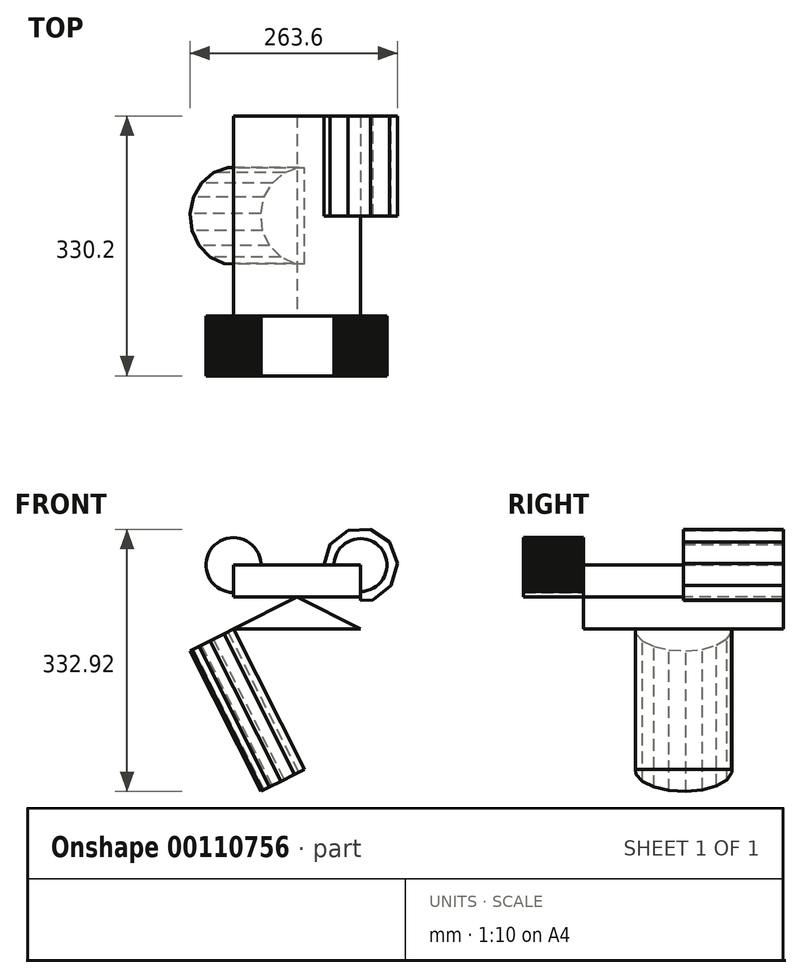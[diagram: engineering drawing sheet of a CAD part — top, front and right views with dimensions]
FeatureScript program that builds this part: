
annotation { "Feature Type Name" : "Feature", "Feature Type Description" : "" }
export const myFeature = defineFeature(function(context is Context, id is Id, definition is map)
    precondition{}
    {
        {
            var Q0;
            Q0=qCreatedBy(makeId("Front.planeOp"),FACE);
            var sketch = newSketch(context, id + "F0", { "sketchPlane" : qUnion([Q0])});
            skLineSegment(sketch, "E0", {"start": v(0, 0) * mm, "end": v(-161.37, 0) * mm});
            skLineSegment(sketch, "E1", {"start": v(-161.37, 0) * mm, "end": v(-161.37, -81.28) * mm});
            skLineSegment(sketch, "E2", {"start": v(-161.37, -81.28) * mm, "end": v(0, -81.28) * mm});
            skLineSegment(sketch, "E3", {"start": v(0, -81.28) * mm, "end": v(0, 0) * mm});
            skSolve(sketch);
        }
        {
            var Q0;
            Q0=makeQuery(id+"F0.imprint","IMPRINT",FACE,{"disambiguationData":[TD([[makeQuery(id+"F0.imprint","IMPRINT",EDGE,{"derivedFrom":sQuery(id+"F0.wireOp",EDGE,"E0")}),1.0]])]});
            var sketch = newSketch(context, id + "F1", { "sketchPlane" : qUnion([Q0])});
            skSolve(sketch);
        }
        {
            var Q0;
            Q0=makeQuery(id+"F0.imprint","IMPRINT",FACE,{"disambiguationData":[TD([[makeQuery(id+"F0.imprint","IMPRINT",EDGE,{"derivedFrom":sQuery(id+"F0.wireOp",EDGE,"E0")}),1.0]])]});
            extrude(context, id + "F2", {"entities" : qUnion([Q0]), "depth" : 254 * mm});
        }
        {
            var Q0;
            Q0=makeQuery(id+"F2.opExtrude","CAP_FACE",FACE,{"disambiguationData":[OSD([sQuery(id+"F0.wireOp",EDGE,"E0"),sQuery(id+"F0.wireOp",EDGE,"E1"),sQuery(id+"F0.wireOp",EDGE,"E2"),sQuery(id+"F0.wireOp",EDGE,"E3")])],"isStart":false});
            var sketch = newSketch(context, id + "F3", { "sketchPlane" : qUnion([Q0])});
            skLineSegment(sketch, "E4", {"start": v(-161.37, -81.28) * mm, "end": v(-161.37, -40.64) * mm});
            skLineSegment(sketch, "E5", {"start": v(-161.37, -40.64) * mm, "end": v(0, -40.64) * mm});
            skLineSegment(sketch, "E6", {"start": v(0, -40.64) * mm, "end": v(0, -81.28) * mm});
            skLineSegment(sketch, "E7", {"start": v(0, -81.28) * mm, "end": v(-80.69, -40.64) * mm});
            skLineSegment(sketch, "E8", {"start": v(-80.69, -40.64) * mm, "end": v(-161.37, -81.28) * mm});
            skSolve(sketch);
        }
        {
            var Q0;
            {var subQ0=sQuery(id+"F3.wireOp",EDGE,"E4");Q0=makeQuery(id+"F3.imprint","IMPRINT",FACE,{"disambiguationData":[TD([[makeQuery(id+"F3.imprint","IMPRINT",EDGE,{"derivedFrom":subQ0}),1.0]])]});}
            extrude(context, id + "F4", {"entities" : qUnion([Q0]), "operationType" : NewBodyOperationType.REMOVE, "endBound" : BoundingType.THROUGH_ALL, "oppositeDirection" : true, "depth" : 25.4 * mm});
        }
        {
            var Q0;
            Q0=makeQuery(id+"F2.opExtrude","CAP_FACE",FACE,{"disambiguationData":[OSD([sQuery(id+"F0.wireOp",EDGE,"E0"),sQuery(id+"F0.wireOp",EDGE,"E1"),sQuery(id+"F0.wireOp",EDGE,"E2"),sQuery(id+"F0.wireOp",EDGE,"E3")])],"isStart":false});
            var sketch = newSketch(context, id + "F5", { "sketchPlane" : qUnion([Q0])});
            skLineSegment(sketch, "E9", {"start": v(-80.69, -40.64) * mm, "end": v(0, -81.28) * mm});
            skLineSegment(sketch, "E10", {"start": v(0, -81.28) * mm, "end": v(0, -40.64) * mm});
            skLineSegment(sketch, "E11", {"start": v(0, -40.64) * mm, "end": v(-80.69, -40.64) * mm});
            skSolve(sketch);
        }
        {
            var Q0;
            Q0=makeQuery(id+"F5.imprint","IMPRINT",FACE,{"disambiguationData":[TD([[makeQuery(id+"F5.imprint","IMPRINT",EDGE,{"derivedFrom":sQuery(id+"F5.wireOp",EDGE,"E9")}),1.0]])]});
            extrude(context, id + "F6", {"entities" : qUnion([Q0]), "operationType" : NewBodyOperationType.REMOVE, "endBound" : BoundingType.THROUGH_ALL, "oppositeDirection" : true, "depth" : 25.4 * mm});
        }
        {
            var Q0;
            {var subQ0=sQuery(id+"F0.wireOp",EDGE,"E1");var subQ1=sQuery(id+"F0.wireOp",EDGE,"E3");var subQ2=sQuery(id+"F0.wireOp",EDGE,"E0");Q0=makeQuery(id+"F6.boolean.opBoolean","SPLIT",FACE,{"disambiguationData":[TD([makeQuery(id+"F2.opExtrude","SWEPT_FACE",FACE,{"disambiguationData":[OSD([subQ2])]})])],"derivedFrom":makeQuery(id+"F2.opExtrude","CAP_FACE",FACE,{"disambiguationData":[OSD([subQ2,subQ0,sQuery(id+"F0.wireOp",EDGE,"E2"),subQ1])],"isStart":false})});}
            var sketch = newSketch(context, id + "F7", { "sketchPlane" : qUnion([Q0])});
            skSolve(sketch);
        }
        {
            var Q0;
            Q0=makeQuery(id+"F7.imprint","IMPRINT",FACE,{"disambiguationData":[TD([[makeQuery(id+"F7.imprint","IMPRINT",EDGE,{"derivedFrom":makeQuery(id+"F2.opExtrude","CAP_EDGE",EDGE,{"disambiguationData":[OSD([sQuery(id+"F0.wireOp",EDGE,"E0")])],"isStart":false})}),1.0]])]});
            var sketch = newSketch(context, id + "F8", { "sketchPlane" : qUnion([Q0])});
            skCircle(sketch, "E12.cCircle", {"center": v(0, 0) * mm, "radius": 33.51 * mm, "construction": true});
            skLineSegment(sketch, "E12.0", {"start": v(-33.51, -2.1) * mm, "end": v(-33.51, 2.1) * mm});
            skLineSegment(sketch, "E12.1", {"start": v(-33.51, 2.1) * mm, "end": v(-32.99, 6.3) * mm});
            skLineSegment(sketch, "E12.2", {"start": v(-32.99, 6.3) * mm, "end": v(-31.94, 10.38) * mm});
            skLineSegment(sketch, "E12.3", {"start": v(-31.94, 10.38) * mm, "end": v(-30.38, 14.3) * mm});
            skLineSegment(sketch, "E12.4", {"start": v(-30.38, 14.3) * mm, "end": v(-28.35, 18) * mm});
            skLineSegment(sketch, "E12.5", {"start": v(-28.35, 18) * mm, "end": v(-25.87, 21.4) * mm});
            skLineSegment(sketch, "E12.6", {"start": v(-25.87, 21.4) * mm, "end": v(-22.99, 24.48) * mm});
            skLineSegment(sketch, "E12.7", {"start": v(-22.99, 24.48) * mm, "end": v(-19.74, 27.17) * mm});
            skLineSegment(sketch, "E12.8", {"start": v(-19.74, 27.17) * mm, "end": v(-16.18, 29.43) * mm});
            skLineSegment(sketch, "E12.9", {"start": v(-16.18, 29.43) * mm, "end": v(-12.36, 31.22) * mm});
            skLineSegment(sketch, "E12.10", {"start": v(-12.36, 31.22) * mm, "end": v(-8.35, 32.53) * mm});
            skLineSegment(sketch, "E12.11", {"start": v(-8.35, 32.53) * mm, "end": v(-4.2, 33.32) * mm});
            skLineSegment(sketch, "E12.12", {"start": v(-4.2, 33.32) * mm, "end": v(0, 33.58) * mm});
            skLineSegment(sketch, "E12.13", {"start": v(0, 33.58) * mm, "end": v(4.2, 33.32) * mm});
            skLineSegment(sketch, "E12.14", {"start": v(4.2, 33.32) * mm, "end": v(8.35, 32.53) * mm});
            skLineSegment(sketch, "E12.15", {"start": v(8.35, 32.53) * mm, "end": v(12.36, 31.22) * mm});
            skLineSegment(sketch, "E12.16", {"start": v(12.36, 31.22) * mm, "end": v(16.18, 29.43) * mm});
            skLineSegment(sketch, "E12.17", {"start": v(16.18, 29.43) * mm, "end": v(19.74, 27.17) * mm});
            skLineSegment(sketch, "E12.18", {"start": v(19.74, 27.17) * mm, "end": v(22.99, 24.48) * mm});
            skLineSegment(sketch, "E12.19", {"start": v(22.99, 24.48) * mm, "end": v(25.87, 21.4) * mm});
            skLineSegment(sketch, "E12.20", {"start": v(25.87, 21.4) * mm, "end": v(28.35, 18) * mm});
            skLineSegment(sketch, "E12.21", {"start": v(28.35, 18) * mm, "end": v(30.38, 14.3) * mm});
            skLineSegment(sketch, "E12.22", {"start": v(30.38, 14.3) * mm, "end": v(31.94, 10.38) * mm});
            skLineSegment(sketch, "E12.23", {"start": v(31.94, 10.38) * mm, "end": v(32.99, 6.3) * mm});
            skLineSegment(sketch, "E12.24", {"start": v(32.99, 6.3) * mm, "end": v(33.51, 2.1) * mm});
            skLineSegment(sketch, "E12.25", {"start": v(33.51, 2.1) * mm, "end": v(33.51, -2.1) * mm});
            skLineSegment(sketch, "E12.26", {"start": v(33.51, -2.1) * mm, "end": v(32.99, -6.3) * mm});
            skLineSegment(sketch, "E12.27", {"start": v(32.99, -6.3) * mm, "end": v(31.94, -10.38) * mm});
            skLineSegment(sketch, "E12.28", {"start": v(31.94, -10.38) * mm, "end": v(30.38, -14.3) * mm});
            skLineSegment(sketch, "E12.29", {"start": v(30.38, -14.3) * mm, "end": v(28.35, -18) * mm});
            skLineSegment(sketch, "E12.30", {"start": v(28.35, -18) * mm, "end": v(25.87, -21.4) * mm});
            skLineSegment(sketch, "E12.31", {"start": v(25.87, -21.4) * mm, "end": v(22.99, -24.48) * mm});
            skLineSegment(sketch, "E12.32", {"start": v(22.99, -24.48) * mm, "end": v(19.74, -27.17) * mm});
            skLineSegment(sketch, "E12.33", {"start": v(19.74, -27.17) * mm, "end": v(16.18, -29.43) * mm});
            skLineSegment(sketch, "E12.34", {"start": v(16.18, -29.43) * mm, "end": v(12.36, -31.22) * mm});
            skLineSegment(sketch, "E12.35", {"start": v(12.36, -31.22) * mm, "end": v(8.35, -32.53) * mm});
            skLineSegment(sketch, "E12.36", {"start": v(8.35, -32.53) * mm, "end": v(4.2, -33.32) * mm});
            skLineSegment(sketch, "E12.37", {"start": v(4.2, -33.32) * mm, "end": v(0, -33.58) * mm});
            skLineSegment(sketch, "E12.38", {"start": v(0, -33.58) * mm, "end": v(-4.2, -33.32) * mm});
            skLineSegment(sketch, "E12.39", {"start": v(-4.2, -33.32) * mm, "end": v(-8.35, -32.53) * mm});
            skLineSegment(sketch, "E12.40", {"start": v(-8.35, -32.53) * mm, "end": v(-12.36, -31.22) * mm});
            skLineSegment(sketch, "E12.41", {"start": v(-12.36, -31.22) * mm, "end": v(-16.18, -29.43) * mm});
            skLineSegment(sketch, "E12.42", {"start": v(-16.18, -29.43) * mm, "end": v(-19.74, -27.17) * mm});
            skLineSegment(sketch, "E12.43", {"start": v(-19.74, -27.17) * mm, "end": v(-22.99, -24.48) * mm});
            skLineSegment(sketch, "E12.44", {"start": v(-22.99, -24.48) * mm, "end": v(-25.87, -21.4) * mm});
            skLineSegment(sketch, "E12.45", {"start": v(-25.87, -21.4) * mm, "end": v(-28.35, -18) * mm});
            skLineSegment(sketch, "E12.46", {"start": v(-28.35, -18) * mm, "end": v(-30.38, -14.3) * mm});
            skLineSegment(sketch, "E12.47", {"start": v(-30.38, -14.3) * mm, "end": v(-31.94, -10.38) * mm});
            skLineSegment(sketch, "E12.48", {"start": v(-31.94, -10.38) * mm, "end": v(-32.99, -6.3) * mm});
            skLineSegment(sketch, "E12.49", {"start": v(-32.99, -6.3) * mm, "end": v(-33.51, -2.1) * mm});
            skPoint(sketch, "E12.0.midPoint", {"position": v(-33.51, 0) * mm});
            skSolve(sketch);
        }
        {
            var Q0;
            {var subQ1=sQuery(id+"F8.wireOp",EDGE,"E12.1");Q0=makeQuery(id+"F8.imprint","IMPRINT",FACE,{"disambiguationData":[TD([[makeQuery(id+"F8.imprint","IMPRINT",EDGE,{"derivedFrom":subQ1}),-1.0]])]});}
            extrude(context, id + "F9", {"entities" : qUnion([Q0]), "depth" : 76.2 * mm});
        }
        {
            var Q0;
            Q0=makeQuery(id+"F7.imprint","IMPRINT",FACE,{"disambiguationData":[TD([[makeQuery(id+"F7.imprint","IMPRINT",EDGE,{"derivedFrom":makeQuery(id+"F2.opExtrude","CAP_EDGE",EDGE,{"disambiguationData":[OSD([sQuery(id+"F0.wireOp",EDGE,"E0")])],"isStart":false})}),1.0]])]});
            var sketch = newSketch(context, id + "F10", { "sketchPlane" : qUnion([Q0])});
            skCircle(sketch, "E13.cCircle", {"center": v(-161.48, 0) * mm, "radius": 34.82 * mm, "construction": true});
            skLineSegment(sketch, "E13.0", {"start": v(-126.66, 2.2) * mm, "end": v(-126.66, -2.2) * mm});
            skLineSegment(sketch, "E13.1", {"start": v(-126.66, -2.2) * mm, "end": v(-127.21, -6.54) * mm});
            skLineSegment(sketch, "E13.2", {"start": v(-127.21, -6.54) * mm, "end": v(-128.3, -10.78) * mm});
            skLineSegment(sketch, "E13.3", {"start": v(-128.3, -10.78) * mm, "end": v(-129.91, -14.85) * mm});
            skLineSegment(sketch, "E13.4", {"start": v(-129.91, -14.85) * mm, "end": v(-132.02, -18.7) * mm});
            skLineSegment(sketch, "E13.5", {"start": v(-132.02, -18.7) * mm, "end": v(-134.6, -22.24) * mm});
            skLineSegment(sketch, "E13.6", {"start": v(-134.6, -22.24) * mm, "end": v(-137.6, -25.43) * mm});
            skLineSegment(sketch, "E13.7", {"start": v(-137.6, -25.43) * mm, "end": v(-140.97, -28.22) * mm});
            skLineSegment(sketch, "E13.8", {"start": v(-140.97, -28.22) * mm, "end": v(-144.67, -30.57) * mm});
            skLineSegment(sketch, "E13.9", {"start": v(-144.67, -30.57) * mm, "end": v(-148.64, -32.44) * mm});
            skLineSegment(sketch, "E13.10", {"start": v(-148.64, -32.44) * mm, "end": v(-152.8, -33.79) * mm});
            skLineSegment(sketch, "E13.11", {"start": v(-152.8, -33.79) * mm, "end": v(-157.1, -34.61) * mm});
            skLineSegment(sketch, "E13.12", {"start": v(-157.1, -34.61) * mm, "end": v(-161.48, -34.89) * mm});
            skLineSegment(sketch, "E13.13", {"start": v(-161.48, -34.89) * mm, "end": v(-165.85, -34.61) * mm});
            skLineSegment(sketch, "E13.14", {"start": v(-165.85, -34.61) * mm, "end": v(-170.15, -33.79) * mm});
            skLineSegment(sketch, "E13.15", {"start": v(-170.15, -33.79) * mm, "end": v(-174.32, -32.44) * mm});
            skLineSegment(sketch, "E13.16", {"start": v(-174.32, -32.44) * mm, "end": v(-178.28, -30.57) * mm});
            skLineSegment(sketch, "E13.17", {"start": v(-178.28, -30.57) * mm, "end": v(-181.98, -28.22) * mm});
            skLineSegment(sketch, "E13.18", {"start": v(-181.98, -28.22) * mm, "end": v(-185.36, -25.43) * mm});
            skLineSegment(sketch, "E13.19", {"start": v(-185.36, -25.43) * mm, "end": v(-188.36, -22.24) * mm});
            skLineSegment(sketch, "E13.20", {"start": v(-188.36, -22.24) * mm, "end": v(-190.93, -18.7) * mm});
            skLineSegment(sketch, "E13.21", {"start": v(-190.93, -18.7) * mm, "end": v(-193.04, -14.85) * mm});
            skLineSegment(sketch, "E13.22", {"start": v(-193.04, -14.85) * mm, "end": v(-194.66, -10.78) * mm});
            skLineSegment(sketch, "E13.23", {"start": v(-194.66, -10.78) * mm, "end": v(-195.75, -6.54) * mm});
            skLineSegment(sketch, "E13.24", {"start": v(-195.75, -6.54) * mm, "end": v(-196.3, -2.2) * mm});
            skLineSegment(sketch, "E13.25", {"start": v(-196.3, -2.2) * mm, "end": v(-196.3, 2.2) * mm});
            skLineSegment(sketch, "E13.26", {"start": v(-196.3, 2.2) * mm, "end": v(-195.75, 6.54) * mm});
            skLineSegment(sketch, "E13.27", {"start": v(-195.75, 6.54) * mm, "end": v(-194.66, 10.78) * mm});
            skLineSegment(sketch, "E13.28", {"start": v(-194.66, 10.78) * mm, "end": v(-193.04, 14.85) * mm});
            skLineSegment(sketch, "E13.29", {"start": v(-193.04, 14.85) * mm, "end": v(-190.93, 18.7) * mm});
            skLineSegment(sketch, "E13.30", {"start": v(-190.93, 18.7) * mm, "end": v(-188.36, 22.24) * mm});
            skLineSegment(sketch, "E13.31", {"start": v(-188.36, 22.24) * mm, "end": v(-185.36, 25.43) * mm});
            skLineSegment(sketch, "E13.32", {"start": v(-185.36, 25.43) * mm, "end": v(-181.98, 28.22) * mm});
            skLineSegment(sketch, "E13.33", {"start": v(-181.98, 28.22) * mm, "end": v(-178.28, 30.57) * mm});
            skLineSegment(sketch, "E13.34", {"start": v(-178.28, 30.57) * mm, "end": v(-174.32, 32.44) * mm});
            skLineSegment(sketch, "E13.35", {"start": v(-174.32, 32.44) * mm, "end": v(-170.15, 33.79) * mm});
            skLineSegment(sketch, "E13.36", {"start": v(-170.15, 33.79) * mm, "end": v(-165.85, 34.61) * mm});
            skLineSegment(sketch, "E13.37", {"start": v(-165.85, 34.61) * mm, "end": v(-161.48, 34.89) * mm});
            skLineSegment(sketch, "E13.38", {"start": v(-161.48, 34.89) * mm, "end": v(-157.1, 34.61) * mm});
            skLineSegment(sketch, "E13.39", {"start": v(-157.1, 34.61) * mm, "end": v(-152.8, 33.79) * mm});
            skLineSegment(sketch, "E13.40", {"start": v(-152.8, 33.79) * mm, "end": v(-148.64, 32.44) * mm});
            skLineSegment(sketch, "E13.41", {"start": v(-148.64, 32.44) * mm, "end": v(-144.67, 30.57) * mm});
            skLineSegment(sketch, "E13.42", {"start": v(-144.67, 30.57) * mm, "end": v(-140.97, 28.22) * mm});
            skLineSegment(sketch, "E13.43", {"start": v(-140.97, 28.22) * mm, "end": v(-137.6, 25.43) * mm});
            skLineSegment(sketch, "E13.44", {"start": v(-137.6, 25.43) * mm, "end": v(-134.6, 22.24) * mm});
            skLineSegment(sketch, "E13.45", {"start": v(-134.6, 22.24) * mm, "end": v(-132.02, 18.7) * mm});
            skLineSegment(sketch, "E13.46", {"start": v(-132.02, 18.7) * mm, "end": v(-129.91, 14.85) * mm});
            skLineSegment(sketch, "E13.47", {"start": v(-129.91, 14.85) * mm, "end": v(-128.3, 10.78) * mm});
            skLineSegment(sketch, "E13.48", {"start": v(-128.3, 10.78) * mm, "end": v(-127.21, 6.54) * mm});
            skLineSegment(sketch, "E13.49", {"start": v(-127.21, 6.54) * mm, "end": v(-126.66, 2.2) * mm});
            skPoint(sketch, "E13.0.midPoint", {"position": v(-126.66, 0) * mm});
            skSolve(sketch);
        }
        {
            var Q0;
            Q0=makeQuery(id+"F7.imprint","IMPRINT",FACE,{"disambiguationData":[TD([[makeQuery(id+"F7.imprint","IMPRINT",EDGE,{"derivedFrom":makeQuery(id+"F2.opExtrude","CAP_EDGE",EDGE,{"disambiguationData":[OSD([sQuery(id+"F0.wireOp",EDGE,"E0")])],"isStart":false})}),1.0]])]});
            var Q1;
            {var subQ5=sQuery(id+"F10.wireOp",EDGE,"E13.13");Q1=makeQuery(id+"F10.imprint","IMPRINT",FACE,{"disambiguationData":[TD([[makeQuery(id+"F10.imprint","IMPRINT",EDGE,{"derivedFrom":subQ5}),-1.0]])]});}
            extrude(context, id + "F11", {"entities" : qUnion([Q0, Q1]), "depth" : 76.2 * mm});
        }
        {
            var Q0;
            Q0=makeQuery(id+"F1.imprint","IMPRINT",FACE,{"disambiguationData":[TD([[makeQuery(id+"F1.imprint","IMPRINT",EDGE,{"derivedFrom":makeQuery(id+"F0.imprint","IMPRINT",EDGE,{"derivedFrom":sQuery(id+"F0.wireOp",EDGE,"E0")})}),1.0]])]});
            var sketch = newSketch(context, id + "F12", { "sketchPlane" : qUnion([Q0])});
            skCircle(sketch, "E14.cCircle", {"center": v(0, 0) * mm, "radius": 44.7 * mm, "construction": true});
            skLineSegment(sketch, "E14.0", {"start": v(46.96, 1.67) * mm, "end": v(38.97, -26.25) * mm});
            skLineSegment(sketch, "E14.1", {"start": v(38.97, -26.25) * mm, "end": v(16.1, -44.15) * mm});
            skLineSegment(sketch, "E14.2", {"start": v(16.1, -44.15) * mm, "end": v(-12.92, -45.18) * mm});
            skLineSegment(sketch, "E14.3", {"start": v(-12.92, -45.18) * mm, "end": v(-37.01, -28.95) * mm});
            skLineSegment(sketch, "E14.4", {"start": v(-37.01, -28.95) * mm, "end": v(-46.96, -1.67) * mm});
            skLineSegment(sketch, "E14.5", {"start": v(-46.96, -1.67) * mm, "end": v(-38.97, 26.25) * mm});
            skLineSegment(sketch, "E14.6", {"start": v(-38.97, 26.25) * mm, "end": v(-16.1, 44.15) * mm});
            skLineSegment(sketch, "E14.7", {"start": v(-16.1, 44.15) * mm, "end": v(12.92, 45.18) * mm});
            skLineSegment(sketch, "E14.8", {"start": v(12.92, 45.18) * mm, "end": v(37.01, 28.95) * mm});
            skLineSegment(sketch, "E14.9", {"start": v(37.01, 28.95) * mm, "end": v(46.96, 1.67) * mm});
            skPoint(sketch, "E14.0.midPoint", {"position": v(42.97, -12.3) * mm});
            skCircle(sketch, "E15.cCircle", {"center": v(-161.22, 0) * mm, "radius": 47.7 * mm, "construction": true});
            skLineSegment(sketch, "E15.0", {"start": v(-111.15, 2.68) * mm, "end": v(-119.13, -27.26) * mm});
            skLineSegment(sketch, "E15.1", {"start": v(-119.13, -27.26) * mm, "end": v(-143.2, -46.8) * mm});
            skLineSegment(sketch, "E15.2", {"start": v(-143.2, -46.8) * mm, "end": v(-174.15, -48.45) * mm});
            skLineSegment(sketch, "E15.3", {"start": v(-174.15, -48.45) * mm, "end": v(-200.16, -31.6) * mm});
            skLineSegment(sketch, "E15.4", {"start": v(-200.16, -31.6) * mm, "end": v(-211.3, -2.68) * mm});
            skLineSegment(sketch, "E15.5", {"start": v(-211.3, -2.68) * mm, "end": v(-203.31, 27.26) * mm});
            skLineSegment(sketch, "E15.6", {"start": v(-203.31, 27.26) * mm, "end": v(-179.25, 46.8) * mm});
            skLineSegment(sketch, "E15.7", {"start": v(-179.25, 46.8) * mm, "end": v(-148.3, 48.45) * mm});
            skLineSegment(sketch, "E15.8", {"start": v(-148.3, 48.45) * mm, "end": v(-122.29, 31.6) * mm});
            skLineSegment(sketch, "E15.9", {"start": v(-122.29, 31.6) * mm, "end": v(-111.15, 2.68) * mm});
            skPoint(sketch, "E15.0.midPoint", {"position": v(-115.14, -12.3) * mm});
            skSolve(sketch);
        }
        {
            var Q0;
            Q0=makeQuery(id+"F12.imprint","IMPRINT",FACE,{"disambiguationData":[TD([[makeQuery(id+"F12.imprint","IMPRINT",EDGE,{"derivedFrom":sQuery(id+"F12.wireOp",EDGE,"E14.0")}),-1.0]])]});
            extrude(context, id + "F13", {"entities" : qUnion([Q0]), "operationType" : NewBodyOperationType.ADD, "depth" : 127 * mm});
        }
        {
            var Q0;
            Q0=makeQuery(id+"F4.boolean.opBoolean","COPY",FACE,{"derivedFrom":makeQuery(id+"F4.opExtrude","SWEPT_FACE",FACE,{"disambiguationData":[OSD([sQuery(id+"F3.wireOp",EDGE,"E8")])]})});
            var sketch = newSketch(context, id + "F14", { "sketchPlane" : qUnion([Q0])});
            skCircle(sketch, "E16.cCircle", {"center": v(-180.69, -127) * mm, "radius": 61.01 * mm, "construction": true});
            skLineSegment(sketch, "E16.0", {"start": v(-194.32, -187.43) * mm, "end": v(-214.17, -179.13) * mm});
            skLineSegment(sketch, "E16.1", {"start": v(-214.17, -179.13) * mm, "end": v(-229.98, -164.53) * mm});
            skLineSegment(sketch, "E16.2", {"start": v(-229.98, -164.53) * mm, "end": v(-239.84, -145.4) * mm});
            skLineSegment(sketch, "E16.3", {"start": v(-239.84, -145.4) * mm, "end": v(-242.57, -124.07) * mm});
            skLineSegment(sketch, "E16.4", {"start": v(-242.57, -124.07) * mm, "end": v(-237.84, -103.08) * mm});
            skLineSegment(sketch, "E16.5", {"start": v(-237.84, -103.08) * mm, "end": v(-226.2, -84.98) * mm});
            skLineSegment(sketch, "E16.6", {"start": v(-226.2, -84.98) * mm, "end": v(-209.09, -71.94) * mm});
            skLineSegment(sketch, "E16.7", {"start": v(-209.09, -71.94) * mm, "end": v(-188.55, -65.55) * mm});
            skLineSegment(sketch, "E16.8", {"start": v(-188.55, -65.55) * mm, "end": v(-167.05, -66.57) * mm});
            skLineSegment(sketch, "E16.9", {"start": v(-167.05, -66.57) * mm, "end": v(-147.2, -74.87) * mm});
            skLineSegment(sketch, "E16.10", {"start": v(-147.2, -74.87) * mm, "end": v(-131.4, -89.47) * mm});
            skLineSegment(sketch, "E16.11", {"start": v(-131.4, -89.47) * mm, "end": v(-121.53, -108.6) * mm});
            skLineSegment(sketch, "E16.12", {"start": v(-121.53, -108.6) * mm, "end": v(-118.8, -129.93) * mm});
            skLineSegment(sketch, "E16.13", {"start": v(-118.8, -129.93) * mm, "end": v(-123.54, -150.92) * mm});
            skLineSegment(sketch, "E16.14", {"start": v(-123.54, -150.92) * mm, "end": v(-135.17, -169.02) * mm});
            skLineSegment(sketch, "E16.15", {"start": v(-135.17, -169.02) * mm, "end": v(-152.29, -182.06) * mm});
            skLineSegment(sketch, "E16.16", {"start": v(-152.29, -182.06) * mm, "end": v(-172.83, -188.45) * mm});
            skLineSegment(sketch, "E16.17", {"start": v(-172.83, -188.45) * mm, "end": v(-194.32, -187.43) * mm});
            skPoint(sketch, "E16.0.midPoint", {"position": v(-204.24, -183.28) * mm});
            skSolve(sketch);
        }
        {
            var Q0;
            {var subQ5=sQuery(id+"F14.wireOp",EDGE,"E16.0");Q0=makeQuery(id+"F14.imprint","IMPRINT",FACE,{"disambiguationData":[TD([[makeQuery(id+"F14.imprint","IMPRINT",EDGE,{"derivedFrom":subQ5}),-1.0]])]});}
            extrude(context, id + "F15", {"entities" : qUnion([Q0]), "oppositeDirection" : true, "depth" : 200 * mm});
        }
    });
